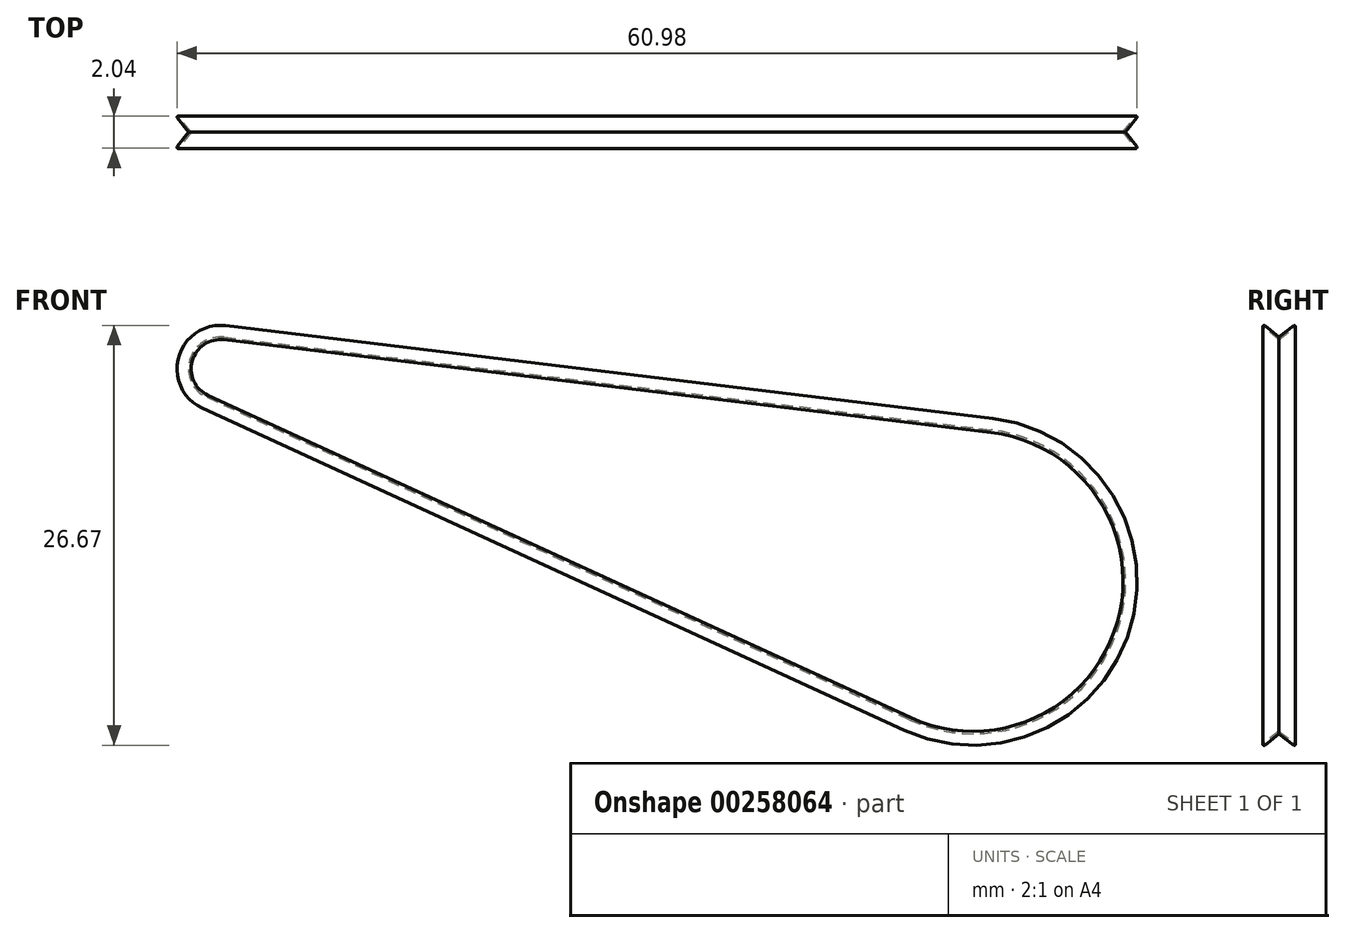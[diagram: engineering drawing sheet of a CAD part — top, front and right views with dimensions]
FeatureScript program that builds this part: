
annotation { "Feature Type Name" : "Feature", "Feature Type Description" : "" }
export const myFeature = defineFeature(function(context is Context, id is Id, definition is map)
    precondition{}
    {
        {
            var Q0;
            Q0=qCreatedBy(makeId("Front.planeOp"),FACE);
            var sketch = newSketch(context, id + "F0", { "sketchPlane" : qUnion([Q0])});
            skArc(sketch, "E0", {"start": v(0.22, 1.84) * mm, "mid": v(-1.78, 0.5) * mm, "end": v(-0.77, -1.69) * mm});
            skArc(sketch, "E1", {"start": v(43.84, -22.16) * mm, "mid": v(56.98, -16.1) * mm, "end": v(48.95, -4.05) * mm});
            skLineSegment(sketch, "E2", {"start": v(0, 0) * mm, "end": v(47.8, -13.5) * mm, "construction": true});
            skLineSegment(sketch, "E3", {"start": v(0.22, 1.84) * mm, "end": v(48.95, -4.05) * mm});
            skLineSegment(sketch, "E4", {"start": v(-0.77, -1.69) * mm, "end": v(43.84, -22.16) * mm});
            skSolve(sketch);
        }
        {
            var Q0;
            Q0=qCreatedBy(makeId("Right.planeOp"),FACE);
            var sketch = newSketch(context, id + "F1", { "sketchPlane" : qUnion([Q0])});
            skLineSegment(sketch, "E5", {"start": v(0, 1.85) * mm, "end": v(0, -2.04) * mm, "construction": true});
            skLineSegment(sketch, "E6", {"start": v(0, 1.85) * mm, "end": v(0, 2.01) * mm, "construction": true});
            skLineSegment(sketch, "E7", {"start": v(0, 2.01) * mm, "end": v(0.92, 2.74) * mm});
            skLineSegment(sketch, "E8", {"start": v(0, 1.85) * mm, "end": v(1, 2.64) * mm});
            skLineSegment(sketch, "E9", {"start": v(1, 2.64) * mm, "end": v(0.92, 2.74) * mm, "construction": true});
            skLineSegment(sketch, "E10", {"start": v(0, 1.85) * mm, "end": v(1.3, 1.85) * mm, "construction": true});
            skArc(sketch, "E11", {"start": v(0.92, 2.74) * mm, "mid": v(1, 2.73) * mm, "end": v(1, 2.64) * mm});
            skArc(sketch, "E12.MirrorCS", {"start": v(-0.92, 2.74) * mm, "mid": v(-1, 2.73) * mm, "end": v(-1, 2.64) * mm});
            skLineSegment(sketch, "E13.MirrorCS", {"start": v(0, 2.01) * mm, "end": v(-0.92, 2.74) * mm});
            skLineSegment(sketch, "E14.MirrorCS", {"start": v(0, 1.85) * mm, "end": v(-1, 2.64) * mm});
            skSolve(sketch);
        }
        {
            var Q0;
            Q0=makeQuery(id+"F1.imprint","IMPRINT",FACE,{"disambiguationData":[TD([[makeQuery(id+"F1.imprint","IMPRINT",EDGE,{"derivedFrom":sQuery(id+"F1.wireOp",EDGE,"E7")}),-1.0]])]});
            var Q1;
            Q1=sQuery(id+"F0.wireOp",EDGE,"E3");
            var Q2;
            Q2=sQuery(id+"F0.wireOp",EDGE,"E1");
            var Q3;
            Q3=sQuery(id+"F0.wireOp",EDGE,"E4");
            var Q4;
            Q4=sQuery(id+"F0.wireOp",EDGE,"E0");
            sweep(context, id + "F2", {"profiles" : qUnion([Q0]), "path" : qUnion([Q1, Q2, Q3, Q4])});
        }
    });
